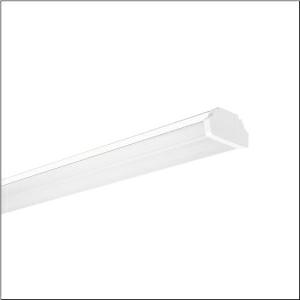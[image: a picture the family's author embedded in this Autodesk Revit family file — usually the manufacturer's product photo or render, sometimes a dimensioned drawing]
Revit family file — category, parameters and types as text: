
# Revit family: dus_r__31_ho_53bd812c1v4105_1de4
name_source: partatom
category: Lighting Fixtures
units: mm (PartAtom-declared; Revit-internal decimal feet)

## family parameters
Cut with Voids When Loaded = No
Host = Face
Light Source = No
Part Type = Normal
Room Calculation Point = No
Round Connector Dimension = Use Diameter
Shared = No

## types (1)
- --- (1 x LED, 10520 lm, 63.8 W, 4000K)
    Apparent Load = 64 VA
    CIE Flux Codes = 47 80 95 92 100
    Color Rendering = 80
    Color Temperature = 4000K
    Default Elevation = 1800 mm
    Description = DUS® 31 HO, luminaire insert, of sheet steel, coil coated, white, length: 1.535mm, width: 81mm, height: 90mm, 5x system unit, system units: 307mm, LED rated luminous flux: 10.520lm, light colour: 840, control gear: ON/OFF Multilumen, CLOi, control gear: ECG Multilumen, with plug, 3-pole, with phase selection, mains connection: 220..240V, AC, 50/60Hz, start of lifetime: 64W, end of service life: 73W, through-wiring accessed according to module size, primary optical cover: cover, of PMMA, light emission: direct distribution, primary light characteristic: symmetric, protection rating (complete): IP20, protection rating (LED compartment): IP50, insulation class (complete): insulation class I (protective earthing), certification: CE, ENEC, VDE, UKCA, impact resistance: IK03, permissible ambient temperature for indoor applications: -35..+35°C, corresponds to IFS (International Featured Standards) requirements for safety and quality in the food industry, reducing of maximum allowable ambient temperature of 5°C with ceiling mounting, packaging unit: 1 piece
    Height = 95 mm
    Lamp = 1 x LED
    Lamp Light Flux = 10520 lm
    Lamp Power = 63.8 W
    Lamp count = 1
    Length = 1535 mm
    Luminous efficacy = 165 lm/W
    Manufacturer = Siteco
    ModVariant = No
    Model = 53BD812C1V4105
    Mounting Place = Ceiling
    Mounting Type = Pendant
    Number of Poles = 1
    OnlyDefault = Yes
    Power Factor = 1
    Product Name = DUS® 31 HO
    Product group = luminaire insert
    ProductGroupID = 901
    Protection Class = Protection class I
    Protection Degree = IP 20
    RLX_Detail_Level = 1
    RLX_Emergency_Light_Flux = 0 lm
    RLX_Emergency_Type = 0
    RLX_Emergency_Type_DB = No
    RlxData = <blob elided: 39905 chars, md5=63e9b9c0>
    Socket = socket
    Standby Power = 0 W
    System Light Flux = 10520 lm
    System Power = 64 W
    Type Comments = factory setting: luminous flux: 100 % | (A | C | E) | 144 mA
    Type Image = l_1003451.jpg
    URL = http://relux.com
    VarID = @adj_138095
    Voltage = 0 V
    Weight = 0.00 kg
    Width = 81 mm

## geometry (parser evidence)
native form markers: Blend x4, Sweep x12
no freeform markers — native parametric forms only
